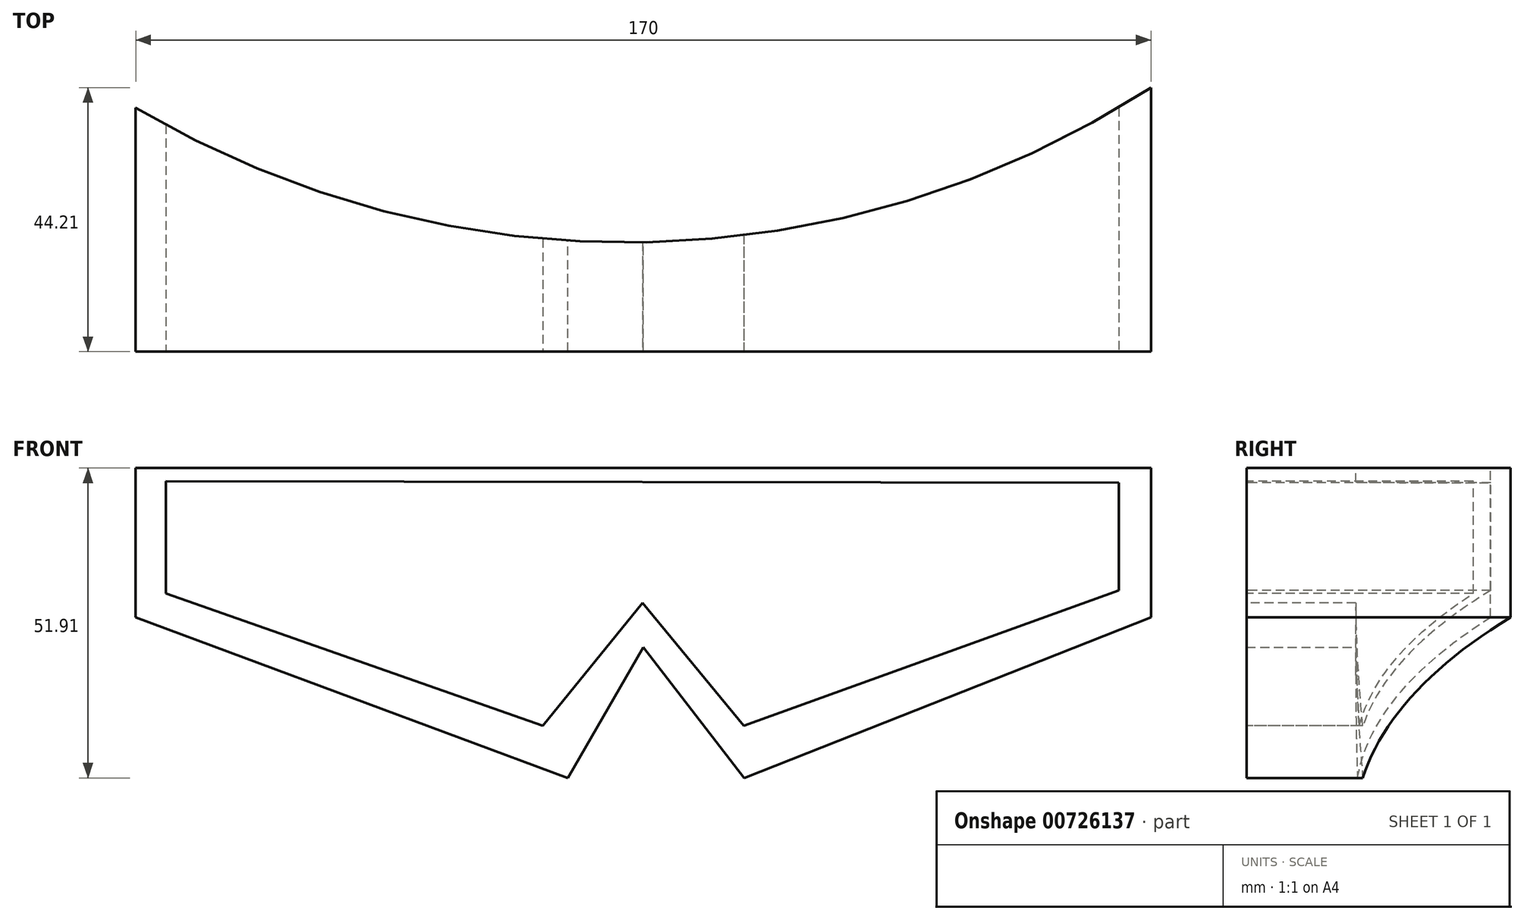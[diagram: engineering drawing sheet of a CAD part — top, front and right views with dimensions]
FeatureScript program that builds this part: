
annotation { "Feature Type Name" : "Feature", "Feature Type Description" : "" }
export const myFeature = defineFeature(function(context is Context, id is Id, definition is map)
    precondition{}
    {
        {
            var Q0;
            Q0=qCreatedBy(makeId("Front.planeOp"),FACE);
            var sketch = newSketch(context, id + "F0", { "sketchPlane" : qUnion([Q0])});
            skLineSegment(sketch, "E0.top", {"start": v(-3.73, 51.9) * mm, "end": v(-88.73, 51.9) * mm});
            skLineSegment(sketch, "E0.left", {"start": v(-3.73, 26.9) * mm, "end": v(-3.73, 51.9) * mm});
            skPoint(sketch, "E1.orphan", {"position": v(-88.73, -8.1) * mm});
            skLineSegment(sketch, "E2.MirrorCS", {"start": v(-173.73, 51.9) * mm, "end": v(-88.73, 51.9) * mm});
            skLineSegment(sketch, "E3.MirrorCS", {"start": v(-173.73, 26.9) * mm, "end": v(-173.73, 51.9) * mm});
            skLineSegment(sketch, "E4", {"start": v(-88.73, 21.9) * mm, "end": v(-71.88, 0) * mm});
            skLineSegment(sketch, "E5", {"start": v(-88.73, 21.9) * mm, "end": v(-101.35, 0) * mm});
            skLineSegment(sketch, "E6", {"start": v(-71.88, 0) * mm, "end": v(-3.73, 26.9) * mm});
            skLineSegment(sketch, "E7", {"start": v(-101.35, 0) * mm, "end": v(-173.73, 26.9) * mm});
            skSolve(sketch);
        }
        {
            var Q0;
            Q0=makeQuery(id+"F0.imprint","IMPRINT",FACE,{"disambiguationData":[TD([[makeQuery(id+"F0.imprint","IMPRINT",EDGE,{"derivedFrom":sQuery(id+"F0.wireOp",EDGE,"E0.top")}),1.0]])]});
            extrude(context, id + "F1", {"entities" : qUnion([Q0]), "depth" : 146 * mm, "offsetDistance" : 25 * mm});
        }
        {
            var Q0;
            Q0=makeQuery(id+"F1.opExtrude","SWEPT_FACE",FACE,{"disambiguationData":[OSD([sQuery(id+"F0.wireOp",EDGE,"E0.top"),sQuery(id+"F0.wireOp",EDGE,"E2.MirrorCS")])]});
            var sketch = newSketch(context, id + "F2", { "sketchPlane" : qUnion([Q0])});
            skArc(sketch, "E8", {"start": v(-245.88, -13.02) * mm, "mid": v(-91.44, -127.71) * mm, "end": v(63, -13.02) * mm});
            skSolve(sketch);
        }
        {
            var Q0;
            {var subQ1=sQuery(id+"F0.wireOp",EDGE,"E0.top");var subQ4=sQuery(id+"F0.wireOp",EDGE,"E2.MirrorCS");var subQ7=makeQuery(id+"F1.opExtrude","CAP_EDGE",EDGE,{"disambiguationData":[OSD([subQ1,subQ4])],"isStart":true});Q0=makeQuery(id+"F2.imprint","IMPRINT",FACE,{"disambiguationData":[TD([[makeQuery(id+"F2.imprint","IMPRINT",EDGE,{"derivedFrom":subQ7}),1.0]])]});}
            extrude(context, id + "F3", {"entities" : qUnion([Q0]), "operationType" : NewBodyOperationType.REMOVE, "oppositeDirection" : true, "depth" : 60 * mm, "offsetDistance" : 25 * mm});
        }
        {
            var Q0;
            Q0=makeQuery(id+"F1.opExtrude","CAP_FACE",FACE,{"disambiguationData":[OSD([sQuery(id+"F0.wireOp",EDGE,"E0.top"),sQuery(id+"F0.wireOp",EDGE,"E0.left"),sQuery(id+"F0.wireOp",EDGE,"E2.MirrorCS"),sQuery(id+"F0.wireOp",EDGE,"E3.MirrorCS"),sQuery(id+"F0.wireOp",EDGE,"E4"),sQuery(id+"F0.wireOp",EDGE,"E5"),sQuery(id+"F0.wireOp",EDGE,"E6"),sQuery(id+"F0.wireOp",EDGE,"E7")])],"isStart":false});
            var sketch = newSketch(context, id + "F4", { "sketchPlane" : qUnion([Q0])});
            skLineSegment(sketch, "E9", {"start": v(-168.67, 49.68) * mm, "end": v(-168.67, 30.9) * mm});
            skLineSegment(sketch, "E10", {"start": v(-168.67, 30.9) * mm, "end": v(-105.56, 8.74) * mm});
            skLineSegment(sketch, "E11", {"start": v(-105.56, 8.74) * mm, "end": v(-88.87, 29.34) * mm});
            skLineSegment(sketch, "E12", {"start": v(-88.87, 29.34) * mm, "end": v(-71.92, 8.74) * mm});
            skLineSegment(sketch, "E13", {"start": v(-71.92, 8.74) * mm, "end": v(-9.08, 31.42) * mm});
            skLineSegment(sketch, "E14", {"start": v(-9.08, 31.42) * mm, "end": v(-9.08, 49.41) * mm});
            skLineSegment(sketch, "E15", {"start": v(-9.08, 49.41) * mm, "end": v(-168.67, 49.68) * mm});
            skSolve(sketch);
        }
        {
            var Q0;
            Q0=makeQuery(id+"F4.imprint","IMPRINT",FACE,{"disambiguationData":[TD([[makeQuery(id+"F4.imprint","IMPRINT",EDGE,{"derivedFrom":sQuery(id+"F4.wireOp",EDGE,"E9")}),1.0]])]});
            extrude(context, id + "F5", {"entities" : qUnion([Q0]), "operationType" : NewBodyOperationType.REMOVE, "oppositeDirection" : true, "depth" : 500 * mm, "offsetDistance" : 25 * mm});
        }
    });
